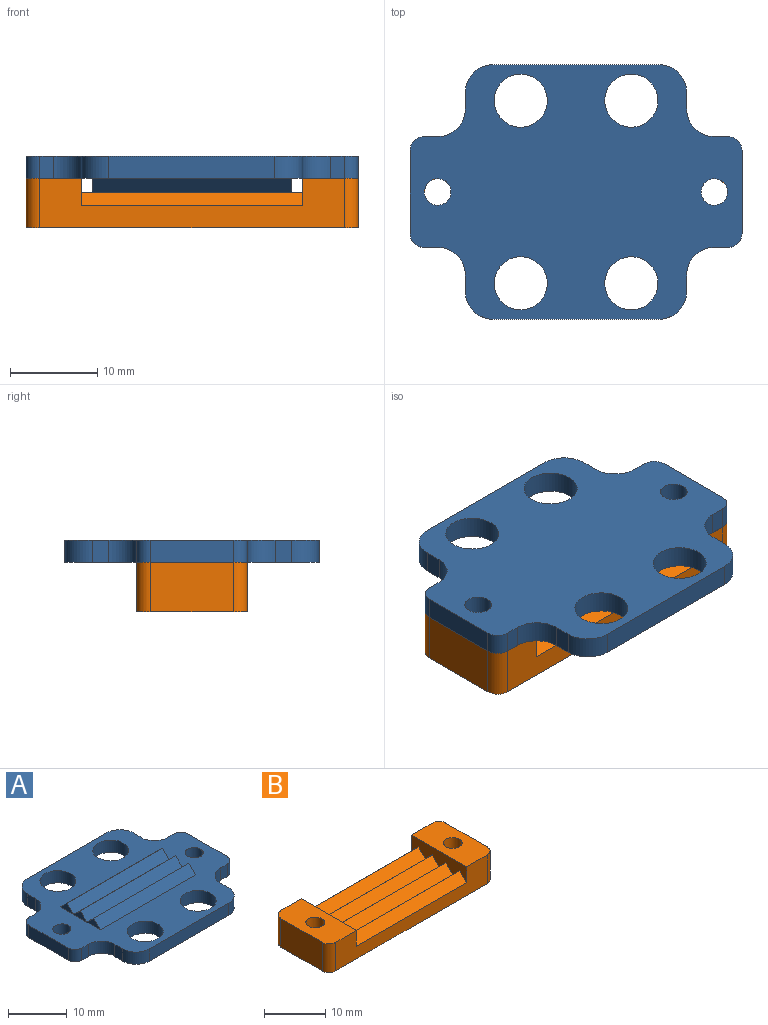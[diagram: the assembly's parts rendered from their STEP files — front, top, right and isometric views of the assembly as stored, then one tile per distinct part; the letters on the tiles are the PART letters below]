
ASSEMBLY  parts=2 mates=1
PART A: 44 faces, bbox 38.1x29.2x4.1 mm
  f0: plane 2.54x1.59mm, normal (0,-1,0), area 4mm2, adj f2,f9,f33,f42
  f1: plane 2.54x1.59mm, normal (0,1,0), area 4mm2, adj f2,f9,f37,f43
  f2: plane 38.1x29.21mm, normal (0,0,1), area 552mm2, adj f0,f1,f3,f4,f5,f6,f7,f8
  f3: plane 2.54x1.59mm, normal (0,1,0), area 4mm2, adj f2,f9,f36,f40
  f4: plane 9.53x2.54mm, normal (-1,0,0), area 24.2mm2, adj f2,f9,f40,f41
  f5: plane 2.54x1.59mm, normal (0,-1,0), area 4mm2, adj f2,f9,f32,f41
  f6: cylinder r=1.52mm len=3.05mm, axis (0,0,-1), area 24.3mm2, adj f2,f9
  f7: cylinder r=1.52mm len=3.05mm, axis (0,0,-1), area 24.3mm2, adj f2,f9
  f8: plane 9.53x2.54mm, normal (1,0,0), area 24.2mm2, adj f2,f9,f42,f43
  f9: plane 38.1x29.21mm, normal (0,0,-1), area 769.7mm2, adj f0,f1,f3,f4,f5,f6,f7,f8
  f10: plane 22.86x1.59mm, normal (0,-0.71,0.71), area 51.3mm2, adj f11,f12,f13,f15
  f11: plane 22.86x1.59mm, normal (0,0.71,0.71), area 51.3mm2, adj f2,f10,f12,f13
  f12: plane 3.18x1.59mm, normal (1,0,0), area 2.5mm2, adj f2,f10,f11
  f13: plane 3.18x1.59mm, normal (-1,0,0), area 2.5mm2, adj f2,f10,f11
  f14: plane 22.86x1.59mm, normal (0,-0.71,0.71), area 51.3mm2, adj f15,f16,f17,f18
  f15: plane 22.86x1.59mm, normal (0,0.71,0.71), area 51.3mm2, adj f10,f14,f16,f17
  f16: plane 3.18x1.59mm, normal (1,0,0), area 2.5mm2, adj f2,f14,f15
  f17: plane 3.18x1.59mm, normal (-1,0,0), area 2.5mm2, adj f2,f14,f15
  f18: plane 22.86x1.59mm, normal (0,0.71,0.71), area 51.3mm2, adj f14,f19,f20,f21
  f19: plane 22.86x1.59mm, normal (0,-0.71,0.71), area 51.3mm2, adj f2,f18,f20,f21
  f20: plane 3.18x1.59mm, normal (1,0,0), area 2.5mm2, adj f2,f18,f19
  f21: plane 3.18x1.59mm, normal (-1,0,0), area 2.5mm2, adj f2,f18,f19
  f22: plane 2.54x1.91mm, normal (-1,0,0), area 4.8mm2, adj f2,f9,f36,f39
  f23: plane 2.54x1.91mm, normal (1,0,0), area 4.8mm2, adj f2,f9,f37,f38
  f24: cylinder r=3.05mm len=6.1mm, axis (0,0,1), area 48.6mm2, adj f2,f9
  f25: plane 19.05x2.54mm, normal (0,1,0), area 48.4mm2, adj f2,f9,f38,f39
  f26: cylinder r=3.05mm len=6.1mm, axis (0,0,1), area 48.6mm2, adj f2,f9
  f27: plane 2.54x1.91mm, normal (-1,0,0), area 4.8mm2, adj f2,f9,f32,f35
  f28: plane 19.05x2.54mm, normal (0,-1,0), area 48.4mm2, adj f2,f9,f34,f35
  f29: plane 2.54x1.91mm, normal (1,0,0), area 4.8mm2, adj f2,f9,f33,f34
  f30: cylinder r=3.05mm len=6.1mm, axis (0,0,1), area 48.6mm2, adj f2,f9
  f31: cylinder r=3.05mm len=6.1mm, axis (0,0,1), area 48.6mm2, adj f2,f9
  f32: cylinder r=3.17mm len=3.18mm, axis (0,0,1), area 12.7mm2, adj f2,f5,f9,f27
  f33: cylinder r=3.17mm len=3.18mm, axis (0,0,-1), area 12.7mm2, adj f0,f2,f9,f29
  f34: cylinder r=3.17mm len=3.18mm, axis (0,0,-1), area 12.7mm2, adj f2,f9,f28,f29
  f35: cylinder r=3.17mm len=3.18mm, axis (0,0,1), area 12.7mm2, adj f2,f9,f27,f28
  f36: cylinder r=3.17mm len=3.18mm, axis (0,0,1), area 12.7mm2, adj f2,f3,f9,f22
  f37: cylinder r=3.17mm len=3.18mm, axis (0,0,-1), area 12.7mm2, adj f1,f2,f9,f23
  f38: cylinder r=3.17mm len=3.18mm, axis (0,0,-1), area 12.7mm2, adj f2,f9,f23,f25
  f39: cylinder r=3.17mm len=3.18mm, axis (0,0,1), area 12.7mm2, adj f2,f9,f22,f25
  f40: cylinder r=1.59mm len=2.54mm, axis (0,0,1), area 6.3mm2, adj f2,f3,f4,f9
  f41: cylinder r=1.59mm len=2.54mm, axis (0,0,-1), area 6.3mm2, adj f2,f4,f5,f9
  f42: cylinder r=1.59mm len=2.54mm, axis (0,0,1), area 6.3mm2, adj f0,f2,f8,f9
  f43: cylinder r=1.59mm len=2.54mm, axis (0,0,-1), area 6.3mm2, adj f1,f2,f8,f9
PART B: 23 faces, bbox 38.1x12.7x5.7 mm
  f0: plane 12.7x3.18mm, normal (1,0,0), area 30.2mm2, adj f3,f5,f7,f9,f10,f11,f12,f13
  f1: plane 12.7x3.18mm, normal (-1,0,0), area 30.2mm2, adj f3,f5,f8,f9,f10,f11,f12,f13
  f2: plane 9.53x5.72mm, normal (1,0,0), area 54.4mm2, adj f6,f8,f19,f22
  f3: plane 34.93x5.72mm, normal (0,1,0), area 119mm2, adj f0,f1,f6,f7,f8,f15,f19,f20
  f4: plane 9.53x5.72mm, normal (-1,0,0), area 54.4mm2, adj f6,f7,f20,f21
  f5: plane 34.93x5.72mm, normal (0,-1,0), area 119mm2, adj f0,f1,f6,f7,f8,f9,f21,f22
  f6: plane 38.1x12.7mm, normal (0,0,-1), area 467.1mm2, adj f2,f3,f4,f5,f17,f18,f19,f20
  f7: plane 12.7x6.35mm, normal (0,0,1), area 72.3mm2, adj f0,f3,f4,f5,f18,f20,f21
  f8: plane 12.7x6.35mm, normal (0,0,1), area 72.3mm2, adj f1,f2,f3,f5,f17,f19,f22
  f9: plane 25.4x1.59mm, normal (0,-0.71,0.71), area 57mm2, adj f0,f1,f5,f10
  f10: plane 25.4x1.59mm, normal (0,0.71,0.71), area 57mm2, adj f0,f1,f9,f11
  f11: plane 25.4x1.59mm, normal (0,-0.71,0.71), area 57mm2, adj f0,f1,f10,f12
  f12: plane 25.4x1.59mm, normal (0,0.71,0.71), area 57mm2, adj f0,f1,f11,f13
  f13: plane 25.4x1.59mm, normal (0,-0.71,0.71), area 57mm2, adj f0,f1,f12,f14
  f14: plane 25.4x1.59mm, normal (0,0.71,0.71), area 57mm2, adj f0,f1,f13,f16
  f15: plane 25.4x1.59mm, normal (0,0.71,0.71), area 57mm2, adj f0,f1,f3,f16
  f16: plane 25.4x1.59mm, normal (0,-0.71,0.71), area 57mm2, adj f0,f1,f14,f15
  f17: cylinder r=1.52mm len=5.72mm, axis (0,0,1), area 54.7mm2, adj f6,f8
  f18: cylinder r=1.52mm len=5.72mm, axis (0,0,1), area 54.7mm2, adj f6,f7
  f19: cylinder r=1.59mm len=5.72mm, axis (0,0,1), area 14.3mm2, adj f2,f3,f6,f8
  f20: cylinder r=1.59mm len=5.72mm, axis (0,0,-1), area 14.3mm2, adj f3,f4,f6,f7
  f21: cylinder r=1.59mm len=5.72mm, axis (0,0,1), area 14.3mm2, adj f4,f5,f6,f7
  f22: cylinder r=1.59mm len=5.72mm, axis (0,0,-1), area 14.3mm2, adj f2,f5,f6,f8
PLACE A rot(axis=(1,0,0),180deg) t=(-6.35,4.76,14.1)mm
PLACE B t=(-6.35,4.76,0)mm
MATE revolute A.f7 <-> B.f17  axis (0,0,-1) through (9.53,4.76,5.72)mm
